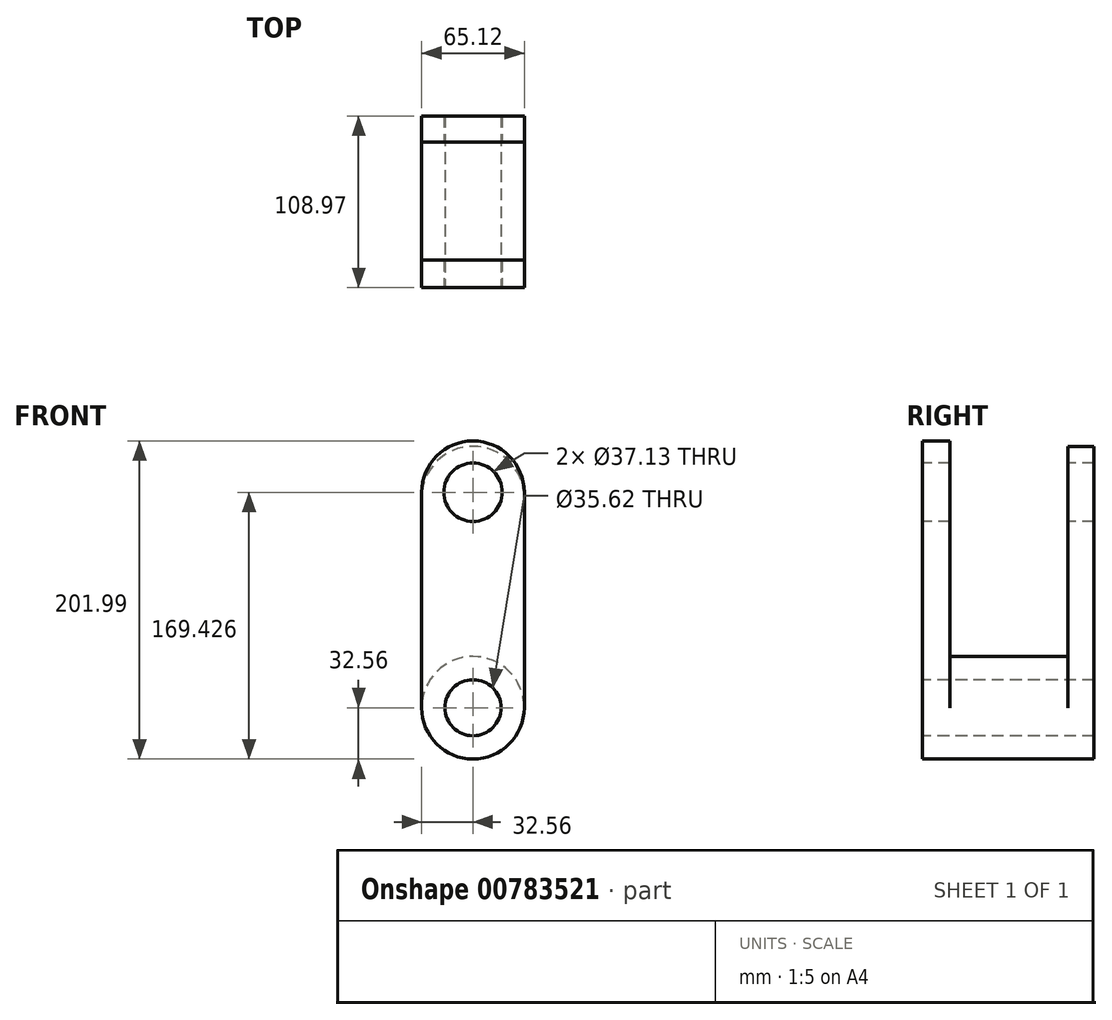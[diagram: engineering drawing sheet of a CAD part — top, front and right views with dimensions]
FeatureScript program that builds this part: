
annotation { "Feature Type Name" : "Feature", "Feature Type Description" : "" }
export const myFeature = defineFeature(function(context is Context, id is Id, definition is map)
    precondition{}
    {
        {
            var Q0;
            Q0=qCreatedBy(makeId("Front.planeOp"),FACE);
            var sketch = newSketch(context, id + "F0", { "sketchPlane" : qUnion([Q0])});
            skCircle(sketch, "E0", {"center": v(0, 0) * mm, "radius": 32.56 * mm});
            skSolve(sketch);
        }
        {
            var Q0;
            Q0=makeQuery(id+"F0.imprint","IMPRINT",FACE,{"disambiguationData":[TD([[makeQuery(id+"F0.imprint","IMPRINT",EDGE,{"derivedFrom":sQuery(id+"F0.wireOp",EDGE,"E0")}),1.0]])]});
            extrude(context, id + "F1", {"entities" : qUnion([Q0]), "depth" : 108.97 * mm, "offsetDistance" : 25.4 * mm});
        }
        {
            var Q0;
            Q0=makeQuery(id+"F1.opExtrude","CAP_FACE",FACE,{"disambiguationData":[OSD([sQuery(id+"F0.wireOp",EDGE,"E0")])],"isStart":true});
            var sketch = newSketch(context, id + "F2", { "sketchPlane" : qUnion([Q0])});
            skLineSegment(sketch, "E1", {"start": v(32.56, 0) * mm, "end": v(32.56, 133.43) * mm});
            skLineSegment(sketch, "E2", {"start": v(-32.56, 0) * mm, "end": v(-32.56, 133.43) * mm});
            skArc(sketch, "E3", {"start": v(32.56, 133.43) * mm, "mid": v(0, 165.99) * mm, "end": v(-32.56, 133.43) * mm});
            skSolve(sketch);
        }
        {
            var Q0;
            {var subQ0=sQuery(id+"F2.wireOp",EDGE,"E1");Q0=makeQuery(id+"F2.imprint","IMPRINT",FACE,{"disambiguationData":[TD([[makeQuery(id+"F2.imprint","IMPRINT",EDGE,{"derivedFrom":subQ0}),1.0]])]});}
            extrude(context, id + "F3", {"entities" : qUnion([Q0]), "operationType" : NewBodyOperationType.ADD, "oppositeDirection" : true, "depth" : 16.76 * mm, "offsetDistance" : 25.4 * mm});
        }
        {
            var Q0;
            Q0=makeQuery(id+"F1.opExtrude","CAP_FACE",FACE,{"disambiguationData":[OSD([sQuery(id+"F0.wireOp",EDGE,"E0")])],"isStart":false});
            var sketch = newSketch(context, id + "F4", { "sketchPlane" : qUnion([Q0])});
            skLineSegment(sketch, "E4", {"start": v(-32.56, 0) * mm, "end": v(-32.56, 136.87) * mm});
            skLineSegment(sketch, "E5", {"start": v(32.56, 0) * mm, "end": v(32.56, 136.87) * mm});
            skArc(sketch, "E6", {"start": v(32.56, 136.87) * mm, "mid": v(0, 169.43) * mm, "end": v(-32.56, 136.87) * mm});
            skSolve(sketch);
        }
        {
            var Q0;
            {var subQ0=sQuery(id+"F4.wireOp",EDGE,"E4");Q0=makeQuery(id+"F4.imprint","IMPRINT",FACE,{"disambiguationData":[TD([[makeQuery(id+"F4.imprint","IMPRINT",EDGE,{"derivedFrom":subQ0}),-1.0]])]});}
            extrude(context, id + "F5", {"entities" : qUnion([Q0]), "operationType" : NewBodyOperationType.ADD, "oppositeDirection" : true, "depth" : 17.53 * mm, "offsetDistance" : 25.4 * mm});
        }
        {
            var Q0;
            {var subQ0=sQuery(id+"F0.wireOp",EDGE,"E0");Q0=makeQuery(id+"F5.boolean.opBoolean","MERGE",FACE,{"derivedFrom":[makeQuery(id+"F1.opExtrude","CAP_FACE",FACE,{"disambiguationData":[OSD([subQ0])],"isStart":false}),makeQuery(id+"F5.opExtrude","CAP_FACE",FACE,{"disambiguationData":[OSD([subQ0,sQuery(id+"F4.wireOp",EDGE,"E4"),sQuery(id+"F4.wireOp",EDGE,"E5"),sQuery(id+"F4.wireOp",EDGE,"E6")])],"isStart":true})]});}
            var sketch = newSketch(context, id + "F6", { "sketchPlane" : qUnion([Q0])});
            skCircle(sketch, "E7", {"center": v(0, 136.87) * mm, "radius": 18.57 * mm});
            skCircle(sketch, "E8", {"center": v(0, 0) * mm, "radius": 17.8 * mm});
            skSolve(sketch);
        }
        {
            var Q0;
            Q0=makeQuery(id+"F6.imprint","IMPRINT",FACE,{"disambiguationData":[TD([[makeQuery(id+"F6.imprint","IMPRINT",EDGE,{"derivedFrom":sQuery(id+"F6.wireOp",EDGE,"E7")}),1.0]])]});
            extrude(context, id + "F7", {"entities" : qUnion([Q0]), "operationType" : NewBodyOperationType.REMOVE, "oppositeDirection" : true, "depth" : 188.21 * mm, "offsetDistance" : 25.4 * mm});
        }
        {
            var Q0;
            Q0=makeQuery(id+"F6.imprint","IMPRINT",FACE,{"disambiguationData":[TD([[makeQuery(id+"F6.imprint","IMPRINT",EDGE,{"derivedFrom":sQuery(id+"F6.wireOp",EDGE,"E8")}),1.0]])]});
            extrude(context, id + "F8", {"entities" : qUnion([Q0]), "operationType" : NewBodyOperationType.REMOVE, "oppositeDirection" : true, "depth" : 219.2 * mm, "offsetDistance" : 25.4 * mm});
        }
    });
